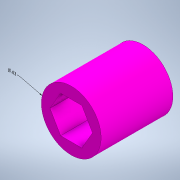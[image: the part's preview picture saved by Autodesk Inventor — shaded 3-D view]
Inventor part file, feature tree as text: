
AUTODESK INVENTOR PART (.ipt)
format: ipt  version: 2022.1 (Build 261234000, 234)  size: 122,880 bytes
history: native  units: in
note: dims shown in document units (in); Inventor stores cm internally (conversion verified against a paired STEP export)
features: other x3, extrude x1, sketch x1
ambient origin geometry x8: Origin, YZ Plane, XZ Plane, XY Plane, X Axis, Y Axis, Z Axis, Center Point
bodies: Solid1 (feature_tree)
feature tree (5):
  other  "Annotations"
  extrude  "Extrusion1"  Depth=0.75in
  other  "Thicken Hex"
  sketch  "Sketch1"  dims[d0=0.375in d2=0.625in d3=0.096in d4=0.75in d5=0.0in d6=0.005in d7=0.005in d8=1.1428in d9=0.625in]
  other  "Diameter Dimension 1"
